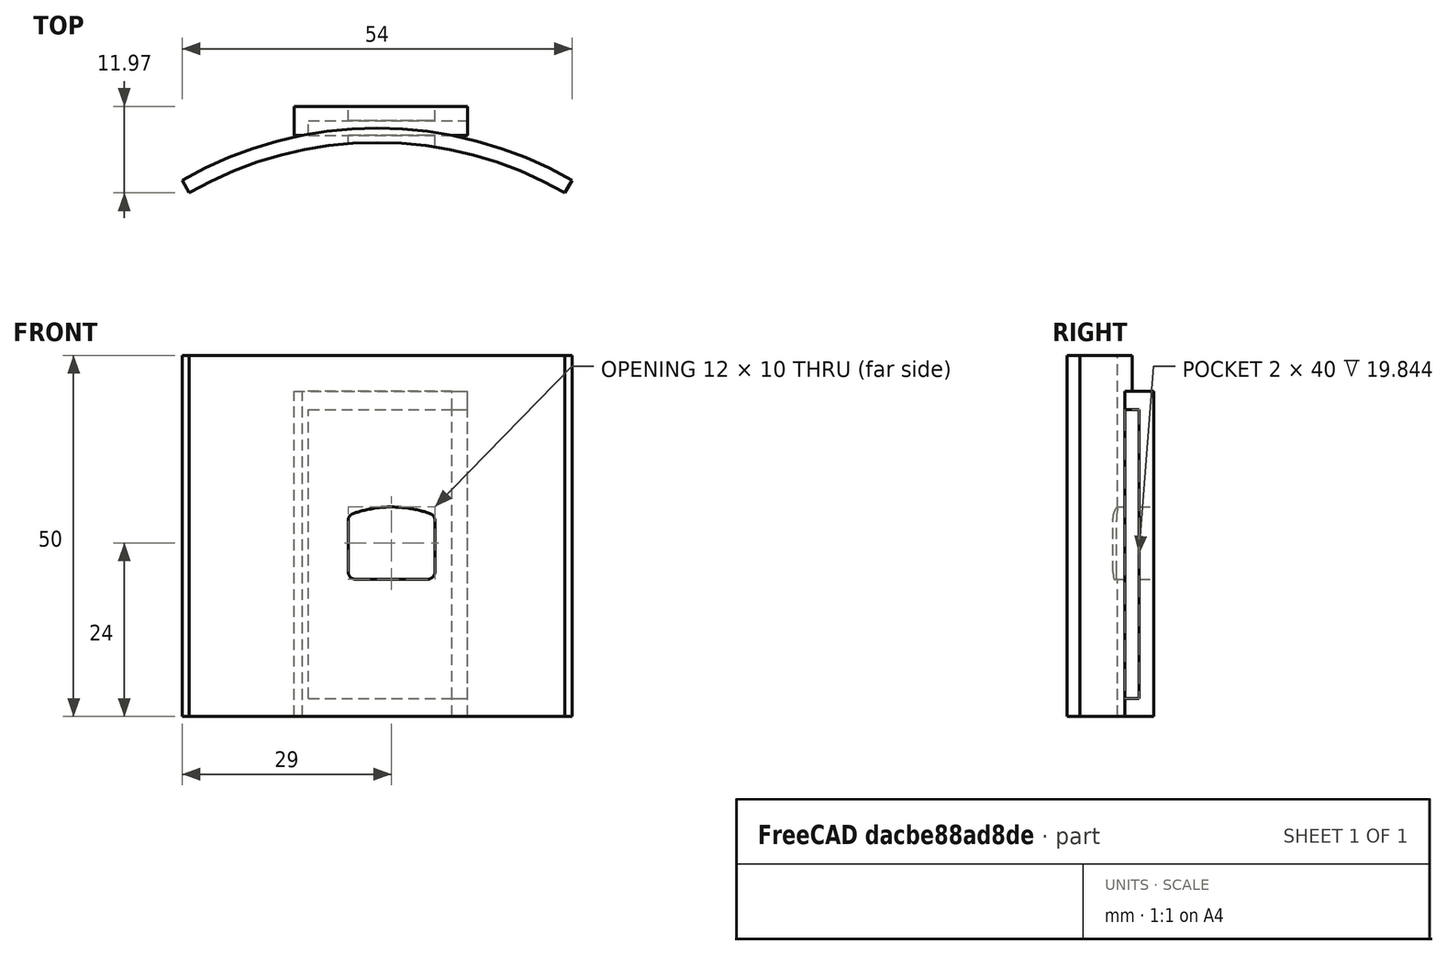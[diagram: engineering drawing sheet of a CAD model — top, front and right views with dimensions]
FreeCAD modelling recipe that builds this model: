
FCSTD DOCUMENT  (FreeCAD 0.16R4924 (Git))
Label: outer_wall_v3
License: All rights reserved
LicenseURL: http://en.wikipedia.org/wiki/All_rights_reserved
objects: Part::Cut×3, Part::MultiFuse×3, Part::Cylinder×2, Part::Box×2, Part::Feature×2, Part::Extrusion×2, Part::Thickness×1
note: 15 computed .brp shape members not serialized (recipe doc carries the construction recipe); baked Part::Feature solids carry a one-line shape summary decoded from their .brp

FEATURE [Part::Cylinder] Cylinder  label="bottle_wall"
  Angle = 60
  Height = 50
  Placement = pos=(8.5,-7,0) rot=(0,0,1;1.0472rad)
  Radius = 54
FEATURE [Part::Cylinder] Cylinder001  label="bottle_wall001"
  Angle = 60
  Height = 50
  Placement = pos=(8.5,-7,0) rot=(0,0,1;1.0472rad)
  Radius = 52
FEATURE [Part::Cut] Cut  label="final_bottle wall"
  Base = -> Cylinder
  Placement = pos=(0,-2,0) rot=(0,0,1;0rad)
  Tool = -> Cylinder001
FEATURE [Part::Box] Box001  label="latch"
  Height = 45
  Length = 24
  Placement = pos=(-3,44,0) rot=(0,0,1;0rad)
  Width = 4
FEATURE [Part::MultiFuse] Fusion
  Shapes = -> [Cut,Box001]
FEATURE [Part::MultiFuse] Fusion001  label="wall_plus_latch"
  Shapes = -> [Fusion,Box001]
FEATURE [Part::Box] Box002  label="slot"
  Height = 40
  Length = 23
  Placement = pos=(-1,44,2.5) rot=(0,0,1;0rad)
  Width = 2
FEATURE [Part::Feature] Common_cs001  label="pin_cs001"
  Placement = pos=(3.5,35,2) rot=(0,0,1;0rad)
  shape: bbox 10 x 2e-07 x 8 mm, 0 faces, 0 solids (baked)
FEATURE [Part::Extrusion] Extrude
  Base = -> Common_cs001
  Dir = (0,6,0)
  Solid = true
FEATURE [Part::Thickness] Thickness
  Faces = -> Extrude [Face7]
  Intersection = false
  Join = 0
  Mode = 0
  SelfIntersection = false
  Value = 1
FEATURE [Part::Feature] Common_cs002  label="pin_cs002"
  Placement = pos=(3.5,35,2) rot=(0,0,1;0rad)
  shape: bbox 10 x 2e-07 x 8 mm, 0 faces, 0 solids (baked)
FEATURE [Part::Extrusion] Extrude001
  Base = -> Common_cs002
  Dir = (0,6,0)
  Solid = true
FEATURE [Part::MultiFuse] Fusion002  label="pin opening"
  Placement = pos=(2,-3,18) rot=(0,0,1;0rad)
  Shapes = -> [Thickness,Extrude,Extrude001]
FEATURE [Part::Cut] Cut003
  Base = -> Fusion001
  Tool = -> Fusion002
FEATURE [Part::Cut] Cut004
  Base = -> Cut003
  Tool = -> Box002
